# Revit family: 0045515 Sylvania Lighting Fixture OPTIX LINEAR RECESSED 1200 TW ALU DA EM
name_source: partatom
category: Lighting Fixtures
revit_build: Autodesk Revit 2017 (Build: 20190507_1515(x64)
units: mm (PartAtom-declared; Revit-internal decimal feet)

## family parameters
Cut with Voids When Loaded = No
Host = Face
Light Source = Yes
OmniClass Number = 23.80.70.00
OmniClass Title = Lighting
Part Type = Normal
Room Calculation Point = No
Round Connector Dimension = Use Diameter
Shared = No

## types (1)
- 0045515 OPTIX LIN R 1200 TW ALU DA EM
    Apparent Load = 24 VA
    Assembly Code = D5020200
    AssetType = Fixed
    ClassificationName = Uniclass2015
    ClassificationValue = EF_70_80
    Color Filter = 16777215
    Cost = 0 $
    Default Elevation = 1219 mm
    Description = OPTIX LINEAR RECESSED 1200 TW ALU DA EM is a high efficacy low glare linear luminaire for office and education applications. Suitable for continuous  light line installations with accessories separately available. Ceiling recessed 1146x95x90 mm. Aluminised plastic extra low glare optics in a single line configuration. White RAL9016 fixture body. 3hr maintained emergency version with DALI monitoring capability. DALI DT8 colour control and dimming. Tunable white colour 2700-6500K, CRI>80, chromaticity tolerance of 3-step MacAdam ellipse. Luminous flux 3650lm. Power consumption 30W. Luminaire efficacy 122lm/W. Lumen maintenance of L90B50 = 40000h. UGR<19, Luminance at 65°<400 Cd/m2, IK07, IP20. Ultra Low Flicker: <5% Photobiological safety risk group 1. Electrical protection Class I. Glow wire test 850°C. Suitable for use with Linect quick connection sytems.
    Dimming Lamp Color Temperature Shift = <None>
    DocumentationLiterature = http://www.sylvania-lighting.com
    DurationUnit = hours
    Emit Shape Visible in Rendering = No
    Emit from Circle Diameter = 610 mm
    ExpectedLife = 50000
    Height = 86 mm  [stored 0.282152 ft]
    IfcExportAs = 92
    IfcExportType = IfcLightFixtureType
    ImpactProtectionIndex = Class I
    InputNominalFrequency = IK07
    InputVoltage = IP20
    Keynote = 0
    LampMacAdamStep = 16500
    LampNominalLuminous = LED
    Length = 1145 mm  [stored 3.75656 ft]
    LightOutputRatio = 3
    LuminaireType = 2200 lm
    Manufacturer = Feilo Sylvania
    ManufacturerName = Feilo Sylvania
    Material_1_SYL = <By Category>
    Material_2_SYL = <By Category>
    Material_3_SYL = <By Category>
    Material_4_SYL = <By Category>
    Model = OPTIX LINEAR RECESSED 1200 TW ALU DA EM
    ModelNumber = 0045515
    ModelReference = OPTIX LINEAR RECESSED 1200 TW ALU DA EM
    Name = OPTIX LINEAR RECESSED 1200 TW ALU DA EM
    NominalDepth = 0 mm  [stored 0 ft]
    NominalHeight = 0 mm  [stored 0 ft]
    NominalLength = 0 mm  [stored 0 ft]
    Photometric Web File = 0045515.ies
    PowerConsumption = 1169
    PowerFactor = 0
    Tilt Angle = -90.00°
    Type Image = <None>
    TypeName = OPTIX LINEAR RECESSED 1200 TW ALU DA EM
    URL = http://www.sylvania-lighting.com
    Voltage = 0 V
    WarrantyDescription = 0
    WarrantyDurationUnit = http://www.sylvania-lighting.com
    Width = 95 mm  [stored 0.31168 ft]

note: [stored X ft] marks values corroborated as IEEE doubles in the binary element streams (Revit-internal decimal feet)

## geometry (parser evidence)
native form markers: Sweep x3
no freeform markers — native parametric forms only
